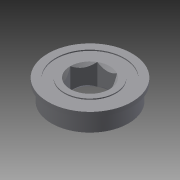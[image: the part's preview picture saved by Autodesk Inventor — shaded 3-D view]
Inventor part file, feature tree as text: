
AUTODESK INVENTOR PART (.ipt)
format: ipt  version: 2013 (Build 170138000, 138)  size: 153,088 bytes
history: native  units: in
note: dims shown in document units (in); Inventor stores cm internally (conversion verified against a paired STEP export)
features: sketch x3, hole x2, other x1, extrude x1, chamfer x1, imported_body x1
ambient origin geometry x8: Origin, YZ Plane, XZ Plane, XY Plane, X Axis, Y Axis, Z Axis, Center Point
feature tree (9):
  other  "Cut-Extrude1"
  extrude  "Extrusion1"  Depth=0.015in TaperAngle=0.0deg
  chamfer  "Chamfer1"  Distance=0.015in Angle=45.0deg
  hole  "Hole5"  [1 undecoded]
  hole  "Hole6"  [1 undecoded]
  imported_body  "Base1"
  sketch  "Sketch3"  dims[d14=0.75in d15=0.015in d16=0.0in d17=0.015in d18=0.125in d19=45.0deg]
  sketch  "Sketch7"  dims[d38=0.25in d39=0.75in d40=0.578in d41=0.25in d42=0.5635in d43=1.0in d44=0.8108in]
  sketch  "Sketch8"  dims[d45=0.25in d46=0.75in d47=0.578in d48=0.25in d49=0.5635in d50=1.0in d51=0.8108in d20=1.0in d21=1.0in]
note: 2 required parameter values undecoded (feature->parameter linkage not recoverable at this tier; creation-order binding heuristic only, values carry confidence <= 0.55)
